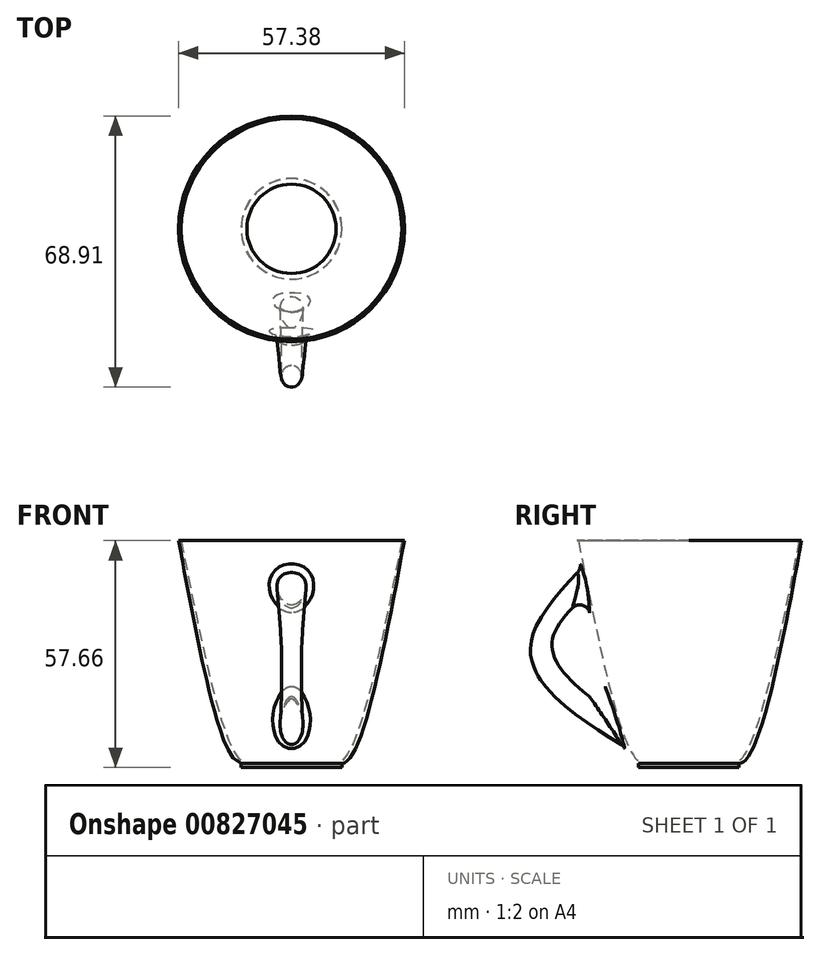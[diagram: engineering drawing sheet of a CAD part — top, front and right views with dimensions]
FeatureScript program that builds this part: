
annotation { "Feature Type Name" : "Feature", "Feature Type Description" : "" }
export const myFeature = defineFeature(function(context is Context, id is Id, definition is map)
    precondition{}
    {
        {
            var Q0;
            Q0=qCreatedBy(makeId("Top.planeOp"),FACE);
            var sketch = newSketch(context, id + "F0", { "sketchPlane" : qUnion([Q0])});
            skCircle(sketch, "E0", {"center": v(0, 0) * mm, "radius": 11.34 * mm});
            skSolve(sketch);
        }
        {
            var Q0;
            Q0=qCreatedBy(makeId("Top.planeOp"),FACE);
            var sketch = newSketch(context, id + "F1", { "sketchPlane" : qUnion([Q0])});
            skCircle(sketch, "E1", {"center": v(0, 0) * mm, "radius": 12.77 * mm});
            skSolve(sketch);
        }
        {
            var Q0;
            Q0=qCreatedBy(makeId("Top.planeOp"),FACE);
            cPlane(context, id + "F2", {"entities" : qUnion([Q0]), "cplaneType" : CPlaneType.OFFSET, "offset" : 56.64 * mm, "width" : 152.4 * mm, "height" : 152.4 * mm});
        }
        {
            var Q0;
            Q0=qCreatedBy(id+"F2.planeOp",FACE);
            var sketch = newSketch(context, id + "F3", { "sketchPlane" : qUnion([Q0])});
            skCircle(sketch, "E2", {"center": v(0, 0) * mm, "radius": 28.02 * mm});
            skSolve(sketch);
        }
        {
            var Q0;
            Q0=qCreatedBy(id+"F2.planeOp",FACE);
            var sketch = newSketch(context, id + "F4", { "sketchPlane" : qUnion([Q0])});
            skCircle(sketch, "E3", {"center": v(0, 0) * mm, "radius": 28.7 * mm});
            skSolve(sketch);
        }
        {
            var Q0;
            Q0=makeQuery(id+"F1.imprint","IMPRINT",FACE,{"disambiguationData":[TD([[makeQuery(id+"F1.imprint","IMPRINT",EDGE,{"derivedFrom":sQuery(id+"F1.wireOp",EDGE,"E1")}),1.0]])]});
            var Q1;
            Q1=makeQuery(id+"F4.imprint","IMPRINT",FACE,{"disambiguationData":[TD([[makeQuery(id+"F4.imprint","IMPRINT",EDGE,{"derivedFrom":sQuery(id+"F4.wireOp",EDGE,"E3")}),1.0]])]});
            loft(context, id + "F5", {"startCondition" : LoftEndDerivativeType.TANGENT_TO_PROFILE, "startMagnitude" : 1, "sheetProfilesArray" : [{ "sheetProfileEntities" : qUnion([Q0]) }, { "sheetProfileEntities" : qUnion([Q1]) }]});
        }
        {
            var Q0;
            Q0=qCreatedBy(makeId("Top.planeOp"),FACE);
            var sketch = newSketch(context, id + "F6", { "sketchPlane" : qUnion([Q0])});
            skCircle(sketch, "E4", {"center": v(0, 0) * mm, "radius": 12.8 * mm});
            skSolve(sketch);
        }
        {
            var Q0;
            Q0=makeQuery(id+"F6.imprint","IMPRINT",FACE,{"disambiguationData":[TD([[makeQuery(id+"F6.imprint","IMPRINT",EDGE,{"derivedFrom":sQuery(id+"F6.wireOp",EDGE,"E4")}),1.0]])]});
            extrude(context, id + "F7", {"entities" : qUnion([Q0]), "operationType" : NewBodyOperationType.ADD, "oppositeDirection" : true, "depth" : 1.02 * mm, "offsetDistance" : 25.4 * mm});
        }
        {
            var Q0;
            Q0=qCreatedBy(makeId("Front.planeOp"),FACE);
            cPlane(context, id + "F8", {"entities" : qUnion([Q0]), "cplaneType" : CPlaneType.OFFSET, "offset" : 13.06 * mm, "width" : 152.4 * mm, "height" : 152.4 * mm});
        }
        {
            var Q0;
            Q0=qCreatedBy(makeId("Front.planeOp"),FACE);
            cPlane(context, id + "F9", {"entities" : qUnion([Q0]), "cplaneType" : CPlaneType.OFFSET, "offset" : 22.86 * mm, "width" : 152.4 * mm, "height" : 152.4 * mm});
        }
        {
            var Q0;
            Q0=qCreatedBy(id+"F9.planeOp",FACE);
            var sketch = newSketch(context, id + "F10", { "sketchPlane" : qUnion([Q0])});
            skCircle(sketch, "E5", {"center": v(0, 49.87) * mm, "radius": 4.15 * mm});
            skSolve(sketch);
        }
        {
            var Q0;
            Q0=qCreatedBy(id+"F8.planeOp",FACE);
            var sketch = newSketch(context, id + "F11", { "sketchPlane" : qUnion([Q0])});
            skCircle(sketch, "E6", {"center": v(0, 5.44) * mm, "radius": 3.14 * mm});
            skSolve(sketch);
        }
        {
            var Q0;
            Q0=qCreatedBy(id+"F2.planeOp",FACE);
            cPlane(context, id + "F12", {"entities" : qUnion([Q0]), "cplaneType" : CPlaneType.OFFSET, "offset" : 25.4 * mm, "oppositeDirection" : true, "width" : 152.4 * mm, "height" : 152.4 * mm});
        }
        {
            var Q0;
            Q0=qCreatedBy(id+"F12.planeOp",FACE);
            var sketch = newSketch(context, id + "F13", { "sketchPlane" : qUnion([Q0])});
            skCircle(sketch, "E7", {"center": v(0, -37.33) * mm, "radius": 2.66 * mm});
            skSolve(sketch);
        }
        {
            var Q1;
            Q1=makeQuery(id+"F10.imprint","IMPRINT",FACE,{"disambiguationData":[TD([[makeQuery(id+"F10.imprint","IMPRINT",EDGE,{"derivedFrom":sQuery(id+"F10.wireOp",EDGE,"E5")}),1.0]])]});
            var Q2;
            Q2=makeQuery(id+"F13.imprint","IMPRINT",FACE,{"disambiguationData":[TD([[makeQuery(id+"F13.imprint","IMPRINT",EDGE,{"derivedFrom":sQuery(id+"F13.wireOp",EDGE,"E7")}),1.0]])]});
            var Q3;
            Q3=makeQuery(id+"F11.imprint","IMPRINT",FACE,{"disambiguationData":[TD([[makeQuery(id+"F11.imprint","IMPRINT",EDGE,{"derivedFrom":sQuery(id+"F11.wireOp",EDGE,"E6")}),1.0]])]});
            loft(context, id + "F14", {"operationType" : NewBodyOperationType.ADD, "sheetProfilesArray" : [{ "sheetProfileEntities" : qUnion([Q1]) }, { "sheetProfileEntities" : qUnion([Q2]) }, { "sheetProfileEntities" : qUnion([Q3]) }]});
        }
        {
            var Q1;
            Q1 = qSketchRegion(id + "F0", true);
            var Q2;
            Q2 = qSketchRegion(id + "F3", true);
            loft(context, id + "F15", {"operationType" : NewBodyOperationType.REMOVE, "sheetProfilesArray" : [{ "sheetProfileEntities" : qUnion([Q1]) }, { "sheetProfileEntities" : qUnion([Q2]) }]});
        }
        {
            var Q0;
            Q0=makeQuery(id+"F14.boolean.opBoolean","INTERSECT",EDGE,{"disambiguationData":[OD(0.0)],"derivedFrom":[makeQuery(id+"F5.opLoft","SWEPT_FACE",FACE,{"disambiguationData":[OSD([sQuery(id+"F1.wireOp",EDGE,"E1"),sQuery(id+"F4.wireOp",EDGE,"E3")])]}),makeQuery(id+"F14.opLoft","SWEPT_FACE",FACE,{"disambiguationData":[OSD([sQuery(id+"F10.wireOp",EDGE,"E5"),sQuery(id+"F13.wireOp",EDGE,"E7")])]})]});
            fillet(context, id + "F16", {"entities" : qUnion([Q0]), "radius" : 2.54 * mm, "tangentPropagation" : true, "allowEdgeOverflow" : false});
        }
        {
            var Q0;
            Q0=makeQuery(id+"F14.boolean.opBoolean","INTERSECT",EDGE,{"disambiguationData":[OD(1.0)],"derivedFrom":[makeQuery(id+"F5.opLoft","SWEPT_FACE",FACE,{"disambiguationData":[OSD([sQuery(id+"F1.wireOp",EDGE,"E1"),sQuery(id+"F4.wireOp",EDGE,"E3")])]}),makeQuery(id+"F14.opLoft","SWEPT_FACE",FACE,{"disambiguationData":[OSD([sQuery(id+"F10.wireOp",EDGE,"E5"),sQuery(id+"F13.wireOp",EDGE,"E7")])]})]});
            fillet(context, id + "F17", {"entities" : qUnion([Q0]), "radius" : 2.54 * mm, "tangentPropagation" : true, "allowEdgeOverflow" : false});
        }
        {
            var Q1;
            Q1=makeQuery(id+"F3.imprint","IMPRINT",FACE,{"disambiguationData":[TD([[makeQuery(id+"F3.imprint","IMPRINT",EDGE,{"derivedFrom":sQuery(id+"F3.wireOp",EDGE,"E2")}),1.0]])]});
            var Q2;
            Q2=makeQuery(id+"F0.imprint","IMPRINT",FACE,{"disambiguationData":[TD([[makeQuery(id+"F0.imprint","IMPRINT",EDGE,{"derivedFrom":sQuery(id+"F0.wireOp",EDGE,"E0")}),1.0]])]});
            loft(context, id + "F18", {"operationType" : NewBodyOperationType.REMOVE, "endCondition" : LoftEndDerivativeType.TANGENT_TO_PROFILE, "endMagnitude" : 1, "sheetProfilesArray" : [{ "sheetProfileEntities" : qUnion([Q1]) }, { "sheetProfileEntities" : qUnion([Q2]) }]});
        }
    });
